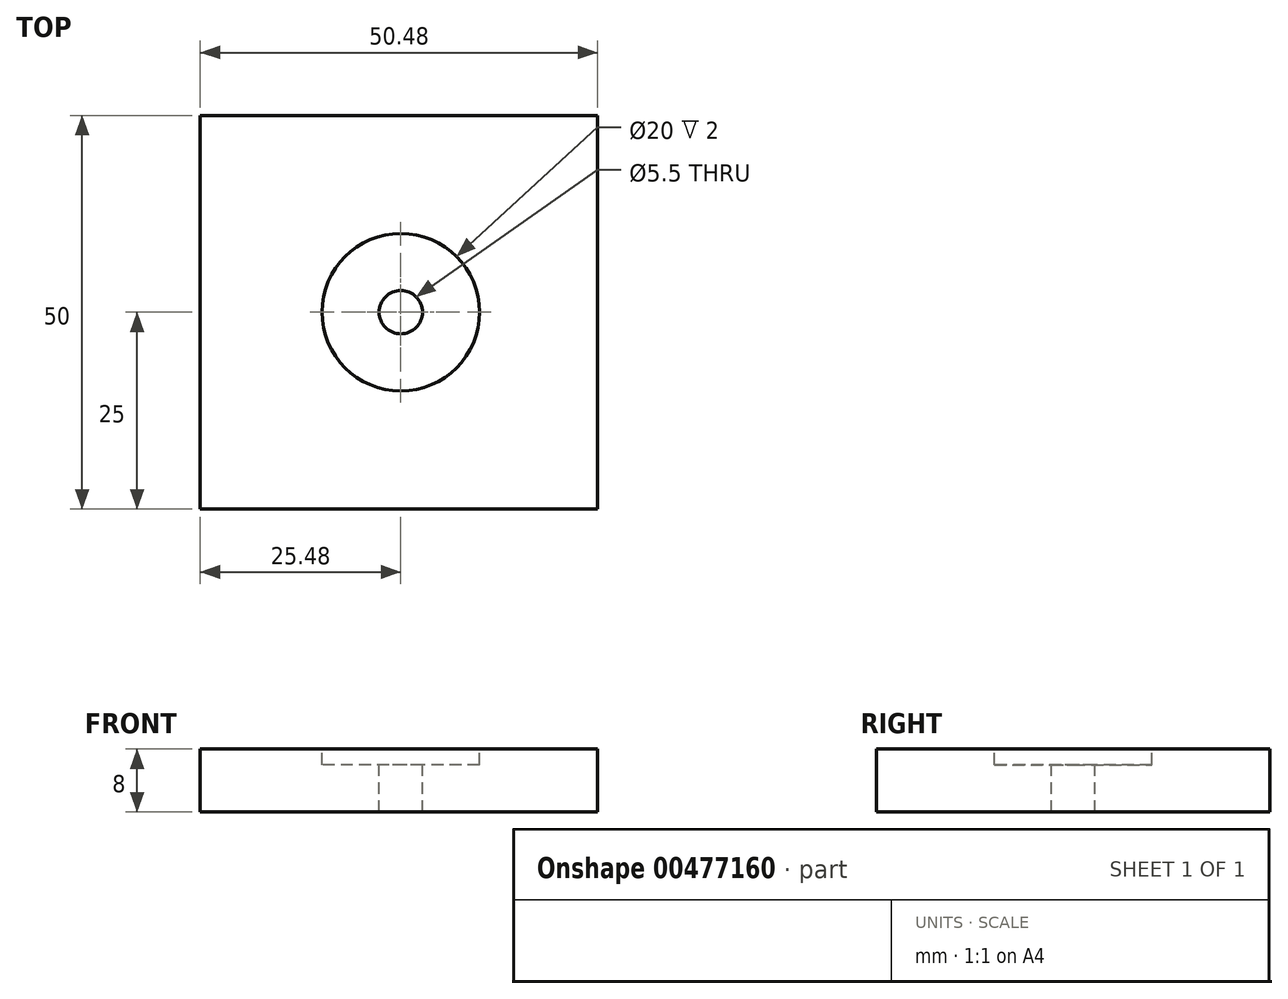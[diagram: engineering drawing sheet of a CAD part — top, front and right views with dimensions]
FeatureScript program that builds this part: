
annotation { "Feature Type Name" : "Feature", "Feature Type Description" : "" }
export const myFeature = defineFeature(function(context is Context, id is Id, definition is map)
    precondition{}
    {
        {
            var Q0;
            Q0=qCreatedBy(makeId("Top.planeOp"),FACE);
            var sketch = newSketch(context, id + "F0", { "sketchPlane" : qUnion([Q0])});
            skLineSegment(sketch, "E0.bottom", {"start": v(-25.48, 25) * mm, "end": v(25, 25) * mm});
            skLineSegment(sketch, "E0.top", {"start": v(-25.48, -25) * mm, "end": v(25, -25) * mm});
            skLineSegment(sketch, "E0.left", {"start": v(-25.48, 25) * mm, "end": v(-25.48, -25) * mm});
            skLineSegment(sketch, "E0.right", {"start": v(25, 25) * mm, "end": v(25, -25) * mm});
            skSolve(sketch);
        }
        {
            var Q0;
            Q0=qSketchRegion(id+"F0",true);
            extrude(context, id + "F1", {"entities" : qUnion([Q0]), "oppositeDirection" : true, "depth" : 8 * mm});
        }
        {
            var Q0;
            Q0=qCreatedBy(makeId("Top.planeOp"),FACE);
            var sketch = newSketch(context, id + "F2", { "sketchPlane" : qUnion([Q0])});
            skCircle(sketch, "E1", {"center": v(0, 0) * mm, "radius": 10 * mm});
            skSolve(sketch);
        }
        {
            var Q0;
            Q0=qSketchRegion(id+"F2",true);
            extrude(context, id + "F3", {"entities" : qUnion([Q0]), "operationType" : NewBodyOperationType.REMOVE, "oppositeDirection" : true, "depth" : 2 * mm});
        }
        {
            var Q0;
            Q0=makeQuery(id+"F3.boolean.opBoolean","COPY",FACE,{"derivedFrom":makeQuery(id+"F3.opExtrude","CAP_FACE",FACE,{"disambiguationData":[OSD([sQuery(id+"F2.wireOp",EDGE,"E1")])],"isStart":false})});
            var sketch = newSketch(context, id + "F4", { "sketchPlane" : qUnion([Q0])});
            skCircle(sketch, "E2", {"center": v(0, 0) * mm, "radius": 2.75 * mm});
            skSolve(sketch);
        }
        {
            var Q0;
            Q0=qSketchRegion(id+"F4",true);
            extrude(context, id + "F5", {"entities" : qUnion([Q0]), "operationType" : NewBodyOperationType.REMOVE, "endBound" : BoundingType.THROUGH_ALL, "oppositeDirection" : true, "depth" : 25 * mm});
        }
    });
